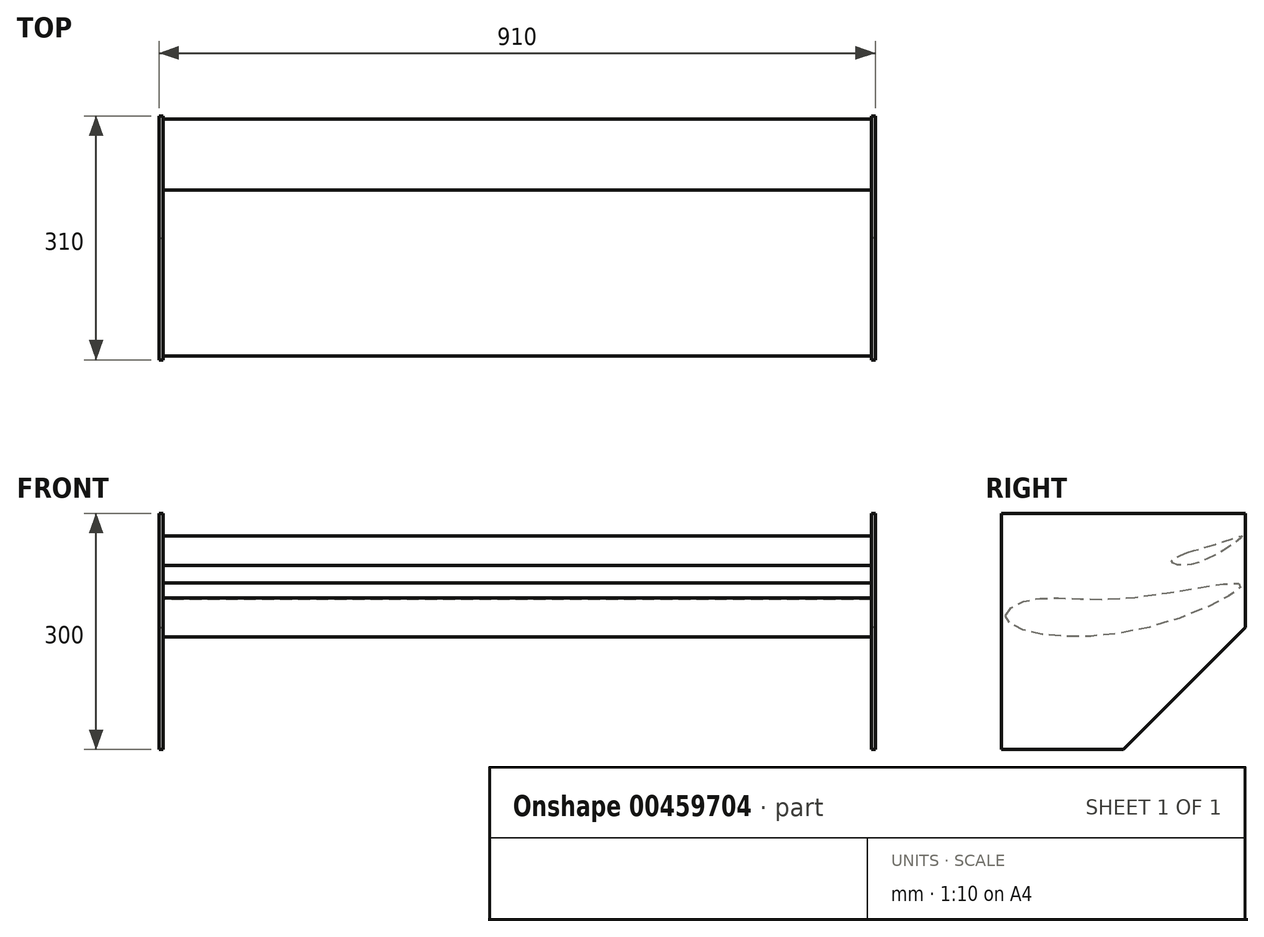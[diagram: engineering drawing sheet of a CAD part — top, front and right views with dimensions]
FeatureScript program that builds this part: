
annotation { "Feature Type Name" : "Feature", "Feature Type Description" : "" }
export const myFeature = defineFeature(function(context is Context, id is Id, definition is map)
    precondition{}
    {
        {
            var Q0;
            Q0=qCreatedBy(makeId("Right.planeOp"),FACE);
            var sketch = newSketch(context, id + "F0", { "sketchPlane" : qUnion([Q0])});
            skFitSpline(sketch, "E0", {"points": [v(-150, 20) * mm, v(-120, 40) * mm, v(0, 42) * mm, v(150, 60) * mm, v(50, 10) * mm, v(-120, 0) * mm, v(-150, 20) * mm]});
            skSolve(sketch);
        }
        {
            var Q0;
            Q0=makeQuery(id+"F0.imprint","IMPRINT",FACE,{"disambiguationData":[TD([[makeQuery(id+"F0.imprint","IMPRINT",EDGE,{"derivedFrom":sQuery(id+"F0.wireOp",EDGE,"E0")}),-1.0]])]});
            extrude(context, id + "F1", {"entities" : qUnion([Q0]), "endBound" : BoundingType.SYMMETRIC, "depth" : 900 * mm, "offsetDistance" : 25 * mm});
        }
        {
            var Q0;
            Q0=makeQuery(id+"F1.opExtrude","CAP_FACE",FACE,{"disambiguationData":[OSD([sQuery(id+"F0.wireOp",EDGE,"E0")])],"isStart":false});
            var sketch = newSketch(context, id + "F2", { "sketchPlane" : qUnion([Q0])});
            skLineSegment(sketch, "E1.bottom", {"start": v(-155, 150) * mm, "end": v(155, 150) * mm});
            skLineSegment(sketch, "E1.top", {"start": v(-155, -150) * mm, "end": v(0, -150) * mm});
            skLineSegment(sketch, "E1.left", {"start": v(-155, 150) * mm, "end": v(-155, -150) * mm});
            skLineSegment(sketch, "E1.right", {"start": v(155, 150) * mm, "end": v(155, 5) * mm});
            skLineSegment(sketch, "E2", {"start": v(0, -150) * mm, "end": v(155, 5) * mm});
            skSolve(sketch);
        }
        {
            var Q0;
            Q0 = qSketchRegion(id + "F2", true);
            extrude(context, id + "F3", {"entities" : qUnion([Q0]), "depth" : 5 * mm, "offsetDistance" : 25 * mm});
        }
        {
            var Q0;
            Q0=makeQuery(id+"F3.opExtrude","SWEPT_BODY",BODY,{"disambiguationData":[OSD([sQuery(id+"F2.wireOp",EDGE,"E1.bottom"),sQuery(id+"F2.wireOp",EDGE,"E1.top"),sQuery(id+"F2.wireOp",EDGE,"E1.left"),sQuery(id+"F2.wireOp",EDGE,"E1.right"),sQuery(id+"F2.wireOp",EDGE,"E2")])]});
            var Q1;
            Q1=qCreatedBy(makeId("Right.planeOp"),FACE);
            mirror(context, id + "F4", {"operationType" : NewBodyOperationType.ADD, "entities" : qUnion([Q0]), "mirrorPlane" : qUnion([Q1])});
        }
        {
            var Q0;
            Q0=qCreatedBy(makeId("Right.planeOp"),FACE);
            var sketch = newSketch(context, id + "F5", { "sketchPlane" : qUnion([Q0])});
            skFitSpline(sketch, "E3", {"points": [v(81.12, 100.14) * mm, v(121.12, 112.14) * mm, v(151.12, 121.14) * mm, v(128.12, 103.93) * mm, v(78.12, 84.14) * mm, v(61.12, 89.14) * mm, v(81.12, 100.14) * mm]});
            skSolve(sketch);
        }
        {
            var Q0;
            Q0 = qSketchRegion(id + "F5", true);
            extrude(context, id + "F6", {"entities" : qUnion([Q0]), "endBound" : BoundingType.SYMMETRIC, "depth" : 900 * mm, "offsetDistance" : 25 * mm});
        }
    });
